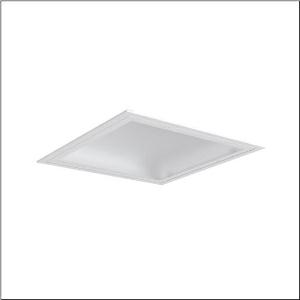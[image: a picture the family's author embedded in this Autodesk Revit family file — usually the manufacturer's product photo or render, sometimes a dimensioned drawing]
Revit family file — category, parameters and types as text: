
# Revit family: mira_21_51fr427a462a
name_source: partatom
category: Lighting Fixtures
units: mm (PartAtom-declared; Revit-internal decimal feet)

## family parameters
Cut with Voids When Loaded = No
Host = Face
Light Source = No
Part Type = Normal
Room Calculation Point = No
Round Connector Dimension = Use Diameter
Shared = No

## types (1)
- Mira 21 (1 x LED, 6420 lm, 53 W, 4000K)
    Apparent Load = 53 VA
    CIE Flux Codes = 50 81 97 100 100
    Color Rendering = 80
    Color Temperature = 4000K
    Default Elevation = 1800 mm
    Description = Mira 21, clean room luminaire, primary light control with reflector, primary optical cover: cover, of PC, light emission: direct distribution, primary light characteristic: symmetric, installation type: recessed, LED, rated luminous flux: 6.420lm, luminous efficacy: 121lm/W, light colour: 840, colour temperature: 4000K, control gear: ON/OFF, with terminal, 3-pole, max. 2.5mm², mains connection: 230V, AC, 50/60Hz, rated input power: 53W, luminaire housing, of sheet steel, coated, pure white (RAL 9010), with concealed spring brackets, module: M625, length: 623mm, width: 623mm, height: 115mm, protection rating (complete): IP54, insulation class (complete): insulation class I (protective earthing), certification: CE, UKCA, permissible operating ambient temperature: -5..+40°C, standard: EN 50419, packaging unit: 1 piece
    Height = 0 mm  [stored 0 ft]
    Lamp = 1 x LED
    Lamp Light Flux = 6420 lm
    Lamp Power = 53 W
    Lamp count = 1
    Length = 625 mm
    Luminous efficacy = 121 lm/W
    Manufacturer = Siteco
    ModVariant = No
    Model = 51FR427A462A
    Mounting Place = Ceiling
    Mounting Type = Recessed
    Number of Poles = 1
    OnlyDefault = Yes
    Power Factor = 1
    Product Name = Mira 21
    Product group = clean room luminaire | ceiling recessed
    ProductGroupID = 402
    Protection Class = Protection class I
    Protection Degree = IP 54
    RLX_Detail_Level = 1
    RLX_Emergency_Light_Flux = 0 lm
    RLX_Emergency_Type = 0
    RLX_Emergency_Type_DB = No
    RlxData = <blob elided: 13385 chars, md5=4e30c675>
    Socket = socket
    Standby Power = 0 W
    System Light Flux = 6420 lm
    System Power = 53 W
    Type Comments = Product without accessories
    Type Image = l_1007109.jpg
    URL = http://relux.com
    VarID = ---
    Voltage = 0 V
    Weight = 0.00 kg
    Width = 625 mm

note: [stored X ft] marks values corroborated as IEEE doubles in the binary element streams (Revit-internal decimal feet)

## geometry (parser evidence)
native form markers: Sweep x10
no freeform markers — native parametric forms only
